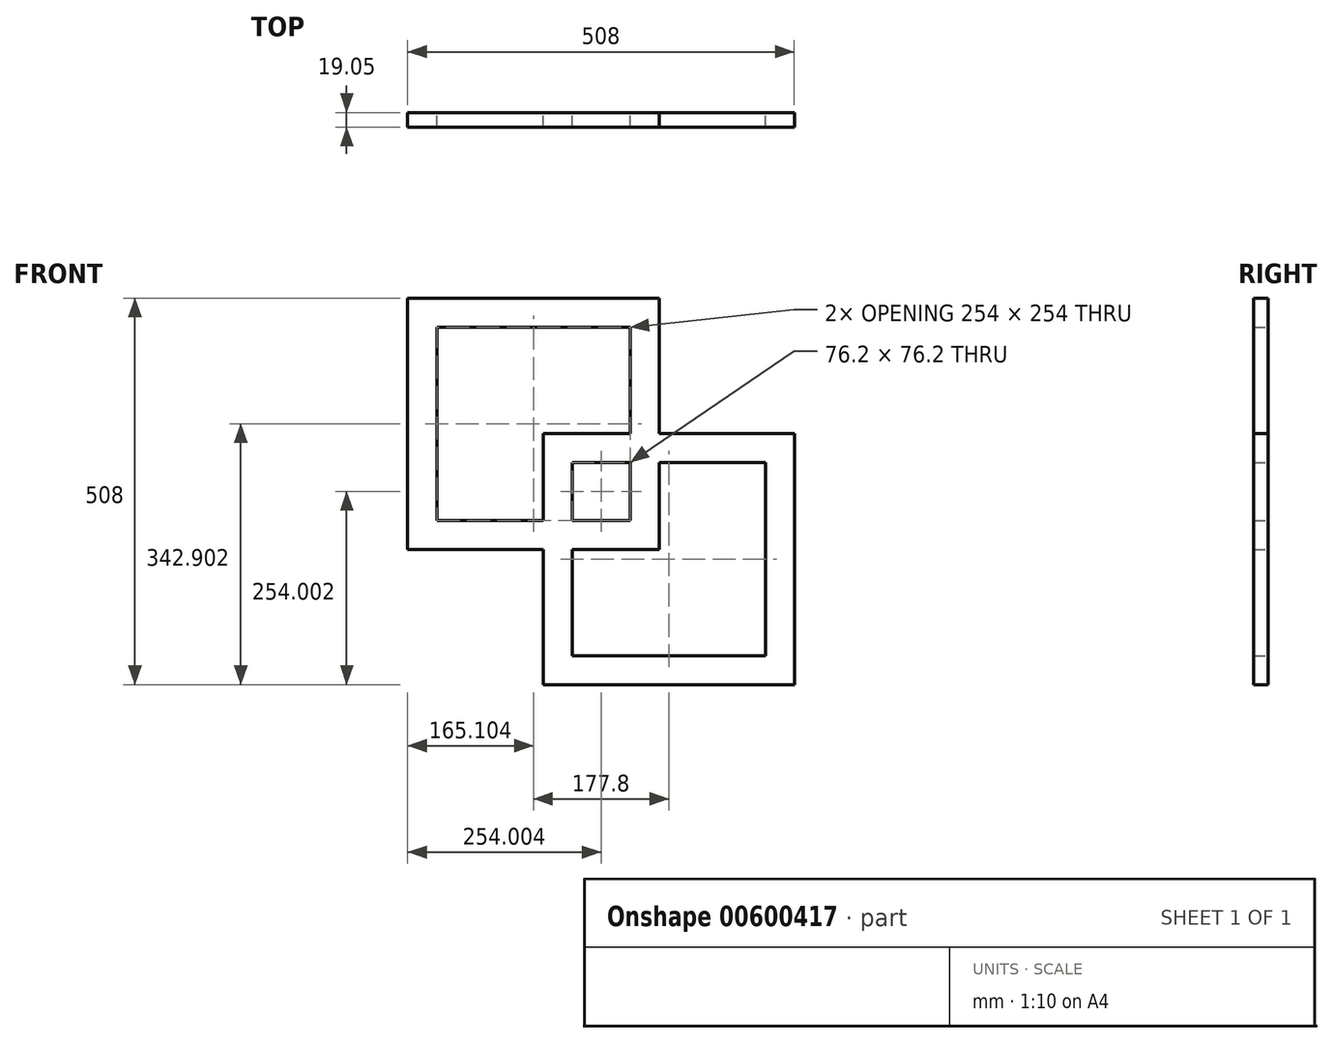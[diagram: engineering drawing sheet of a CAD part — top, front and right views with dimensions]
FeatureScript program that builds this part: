
annotation { "Feature Type Name" : "Feature", "Feature Type Description" : "" }
export const myFeature = defineFeature(function(context is Context, id is Id, definition is map)
    precondition{}
    {
        {
            var Q0;
            Q0=qCreatedBy(makeId("Front.planeOp"),FACE);
            var sketch = newSketch(context, id + "F0", { "sketchPlane" : qUnion([Q0])});
            skLineSegment(sketch, "E0.bottom", {"start": v(-85.97, 41.84) * mm, "end": v(-9.77, 41.84) * mm});
            skLineSegment(sketch, "E0.top", {"start": v(-85.97, -212.16) * mm, "end": v(168.03, -212.16) * mm});
            skLineSegment(sketch, "E0.left", {"start": v(-85.97, 41.84) * mm, "end": v(-85.97, -34.36) * mm});
            skLineSegment(sketch, "E0.right", {"start": v(168.03, 41.84) * mm, "end": v(168.03, -212.16) * mm});
            skLineSegment(sketch, "E1.bottom", {"start": v(-263.77, 219.64) * mm, "end": v(-9.77, 219.64) * mm});
            skLineSegment(sketch, "E1.top", {"start": v(-263.77, -34.36) * mm, "end": v(-124.07, -34.36) * mm});
            skLineSegment(sketch, "E1.left", {"start": v(-263.77, 219.64) * mm, "end": v(-263.77, -34.36) * mm});
            skLineSegment(sketch, "E1.right", {"start": v(-9.77, 219.64) * mm, "end": v(-9.77, 79.94) * mm});
            skLineSegment(sketch, "E2.0", {"start": v(-301.87, 257.74) * mm, "end": v(28.33, 257.74) * mm});
            skLineSegment(sketch, "E2.1", {"start": v(-301.87, 257.74) * mm, "end": v(-301.87, -72.46) * mm});
            skLineSegment(sketch, "E2.2", {"start": v(-301.87, -72.46) * mm, "end": v(-124.07, -72.46) * mm});
            skLineSegment(sketch, "E2.3", {"start": v(28.33, 257.74) * mm, "end": v(28.33, 79.94) * mm});
            skLineSegment(sketch, "E3.0", {"start": v(-124.07, 79.94) * mm, "end": v(-9.77, 79.94) * mm});
            skLineSegment(sketch, "E3.1", {"start": v(-124.07, 79.94) * mm, "end": v(-124.07, -34.36) * mm});
            skLineSegment(sketch, "E3.2", {"start": v(-124.07, -250.26) * mm, "end": v(206.13, -250.26) * mm});
            skLineSegment(sketch, "E3.3", {"start": v(206.13, 79.94) * mm, "end": v(206.13, -250.26) * mm});
            skLineSegment(sketch, "E4.trimOffspring", {"start": v(28.33, 79.94) * mm, "end": v(206.13, 79.94) * mm});
            skLineSegment(sketch, "E5.trimOffspring", {"start": v(28.33, 41.84) * mm, "end": v(168.03, 41.84) * mm});
            skLineSegment(sketch, "E6.trimOffspring", {"start": v(-9.77, 41.84) * mm, "end": v(-9.77, -34.36) * mm});
            skLineSegment(sketch, "E7.trimOffspring", {"start": v(-85.97, -34.36) * mm, "end": v(-9.77, -34.36) * mm});
            skLineSegment(sketch, "E8.trimOffspring", {"start": v(-85.97, -72.46) * mm, "end": v(28.33, -72.46) * mm});
            skLineSegment(sketch, "E9.trimOffspring", {"start": v(-85.97, -72.46) * mm, "end": v(-85.97, -212.16) * mm});
            skLineSegment(sketch, "E10.trimOffspring", {"start": v(-124.07, -72.46) * mm, "end": v(-124.07, -250.26) * mm});
            skLineSegment(sketch, "E11.trimOffspring", {"start": v(28.33, 41.84) * mm, "end": v(28.33, -72.46) * mm});
            skSolve(sketch);
        }
        {
            var Q0;
            Q0 = qSketchRegion(id + "F0", true);
            extrude(context, id + "F1", {"entities" : qUnion([Q0]), "depth" : 19.05 * mm, "offsetDistance" : 25.4 * mm});
        }
    });
